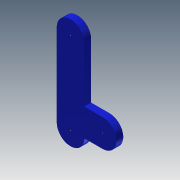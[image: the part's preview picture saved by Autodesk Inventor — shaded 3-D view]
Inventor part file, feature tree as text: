
AUTODESK INVENTOR PART (.ipt)
format: ipt  version: 2013 (Build 170138000, 138)  size: 134,144 bytes
history: native  units: mm
features: extrude x5, sketch x5
ambient origin geometry x8: Origin, YZ Plane, XZ Plane, XY Plane, X Axis, Y Axis, Z Axis, Center Point
bodies: Solid1 (feature_tree)
feature tree (10):
  extrude  "Extrusion1"  Depth=18.0mm
  extrude  "Extrusion2"  Depth=6.0mm
  extrude  "Extrusion3"  Depth=4.0mm
  extrude  "Extrusion4"  Depth=3.0mm
  extrude  "Extrusion5"  Depth=1.5mm TaperAngle=0.0deg
  sketch  "Sketch1"  dims[d0=6.0mm d1=18.0mm]
  sketch  "Sketch2"  dims[d2=6.0mm d4=6.0mm]
  sketch  "Sketch3"  dims[d5=4.0mm d6=4.0mm]
  sketch  "Sketch4"  dims[d7=2.0mm d10=3.0mm]
  sketch  "Sketch5"  dims[d11=6.0mm d12=1.5mm d13=0.0mm d14=3.0mm d15=3.0mm d16=4.0mm d17=6.0mm d18=1.5mm d19=0.0mm d20=4.0mm d21=6.0mm d22=4.0mm d23=1.5mm d24=0.0mm d25=3.0mm d26=1.5mm d27=0.0mm d28=0.2mm d29=0.2mm d30=0.2mm d31=1.5mm d32=0.0mm]
